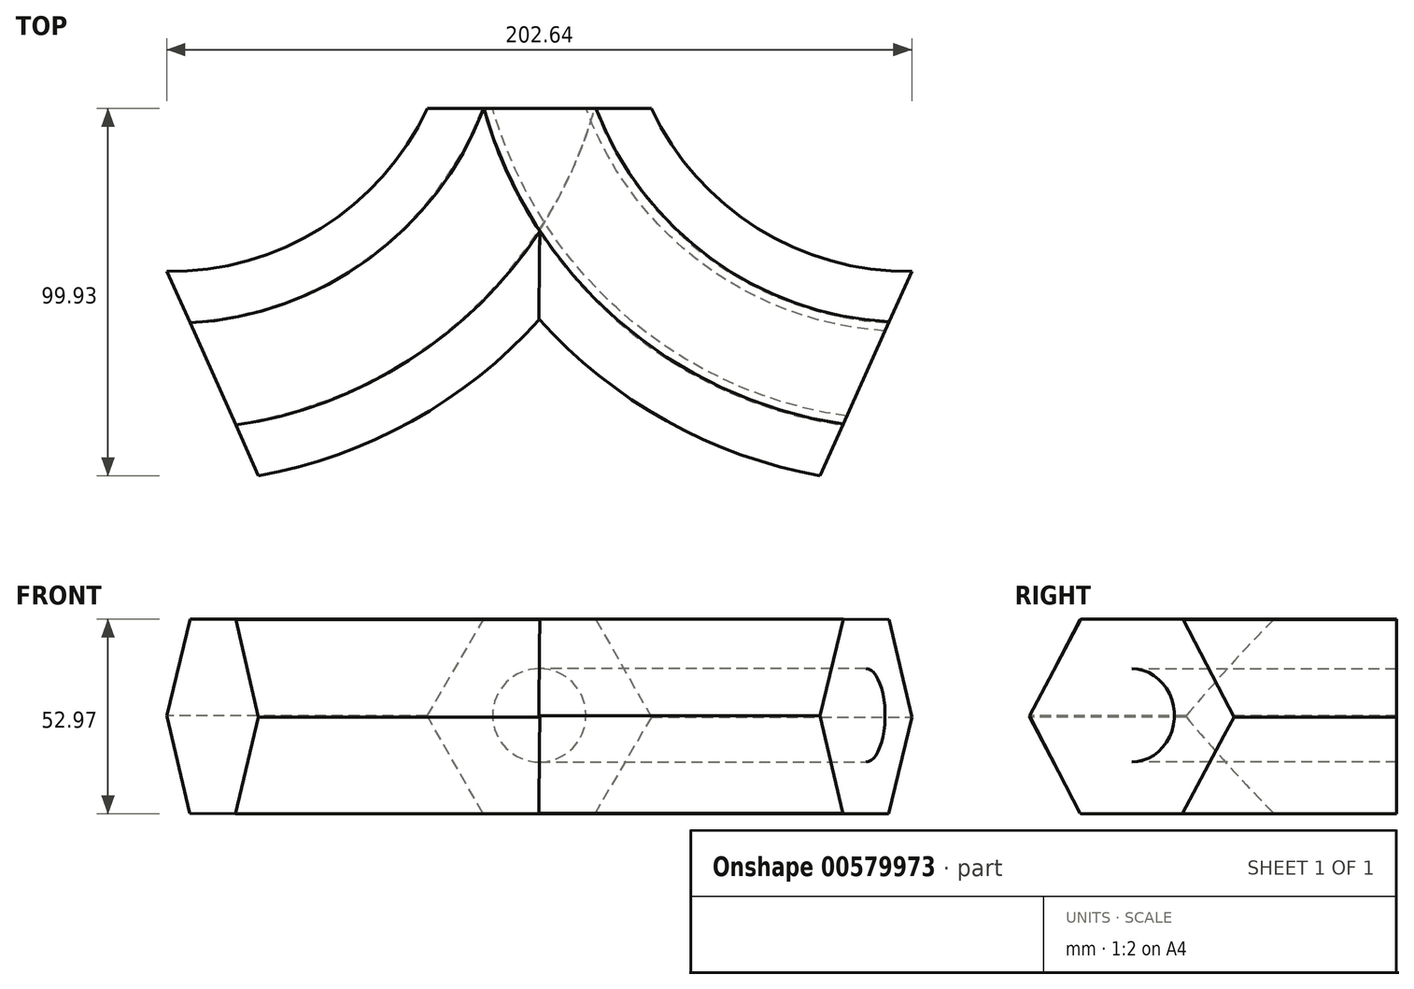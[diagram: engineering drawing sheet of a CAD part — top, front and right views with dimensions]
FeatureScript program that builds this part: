
annotation { "Feature Type Name" : "Feature", "Feature Type Description" : "" }
export const myFeature = defineFeature(function(context is Context, id is Id, definition is map)
    precondition{}
    {
        {
            var Q0;
            Q0=qCreatedBy(makeId("Front.planeOp"),FACE);
            var sketch = newSketch(context, id + "F0", { "sketchPlane" : qUnion([Q0])});
            skCircle(sketch, "E0.cCircle", {"center": v(0, 26.89) * mm, "radius": 26.4 * mm, "construction": true});
            skLineSegment(sketch, "E0.0", {"start": v(-15.4, 0.58) * mm, "end": v(-30.48, 27.07) * mm});
            skLineSegment(sketch, "E0.1", {"start": v(-30.48, 27.07) * mm, "end": v(-15.08, 53.37) * mm});
            skLineSegment(sketch, "E0.2", {"start": v(-15.08, 53.37) * mm, "end": v(15.4, 53.2) * mm});
            skLineSegment(sketch, "E0.3", {"start": v(15.4, 53.2) * mm, "end": v(30.48, 26.7) * mm});
            skLineSegment(sketch, "E0.4", {"start": v(30.48, 26.7) * mm, "end": v(15.08, 0.4) * mm});
            skLineSegment(sketch, "E0.5", {"start": v(15.08, 0.4) * mm, "end": v(-15.4, 0.58) * mm});
            skPoint(sketch, "E0.0.midPoint", {"position": v(-22.94, 13.82) * mm});
            skSolve(sketch);
        }
        {
            var Q0;
            Q0=qCreatedBy(makeId("Top.planeOp"),FACE);
            var sketch = newSketch(context, id + "F1", { "sketchPlane" : qUnion([Q0])});
            skArc(sketch, "E1", {"start": v(-88.86, -72.11) * mm, "mid": v(-33.77, -49.2) * mm, "end": v(0, 0) * mm});
            skArc(sketch, "E2.MirrorCS", {"start": v(88.86, -72.11) * mm, "mid": v(33.77, -49.2) * mm, "end": v(0, 0) * mm});
            skSolve(sketch);
        }
        {
            var Q0;
            Q0=makeQuery(id+"F0.imprint","IMPRINT",FACE,{"disambiguationData":[TD([[makeQuery(id+"F0.imprint","IMPRINT",EDGE,{"derivedFrom":sQuery(id+"F0.wireOp",EDGE,"E0.0")}),-1.0]])]});
            var Q1;
            Q1=sQuery(id+"F1.wireOp",EDGE,"E1");
            sweep(context, id + "F2", {"profiles" : qUnion([Q0]), "path" : qUnion([Q1])});
        }
        {
            var Q0;
            Q0=makeQuery(id+"F0.imprint","IMPRINT",FACE,{"disambiguationData":[TD([[makeQuery(id+"F0.imprint","IMPRINT",EDGE,{"derivedFrom":sQuery(id+"F0.wireOp",EDGE,"E0.0")}),-1.0]])]});
            var Q1;
            Q1=sQuery(id+"F1.wireOp",EDGE,"E2.MirrorCS");
            sweep(context, id + "F3", {"operationType" : NewBodyOperationType.ADD, "profiles" : qUnion([Q0]), "path" : qUnion([Q1])});
        }
        {
            var Q0;
            Q0=makeQuery(id+"F0.imprint","IMPRINT",FACE,{"disambiguationData":[TD([[makeQuery(id+"F0.imprint","IMPRINT",EDGE,{"derivedFrom":sQuery(id+"F0.wireOp",EDGE,"E0.0")}),-1.0]])]});
            var sketch = newSketch(context, id + "F4", { "sketchPlane" : qUnion([Q0])});
            skCircle(sketch, "E3", {"center": v(0, 27.19) * mm, "radius": 12.7 * mm});
            skSolve(sketch);
        }
        {
            var Q0;
            Q0=makeQuery(id+"F4.imprint","IMPRINT",FACE,{"disambiguationData":[TD([[makeQuery(id+"F4.imprint","IMPRINT",EDGE,{"derivedFrom":sQuery(id+"F4.wireOp",EDGE,"E3")}),1.0]])]});
            var Q1;
            Q1=sQuery(id+"F4.wireOp",EDGE,"E3");
            var Q2;
            Q2=sQuery(id+"F1.wireOp",EDGE,"E2.MirrorCS");
            sweep(context, id + "F5", {"operationType" : NewBodyOperationType.REMOVE, "profiles" : qUnion([Q0]), "surfaceProfiles" : qUnion([Q1]), "path" : qUnion([Q2])});
        }
    });
